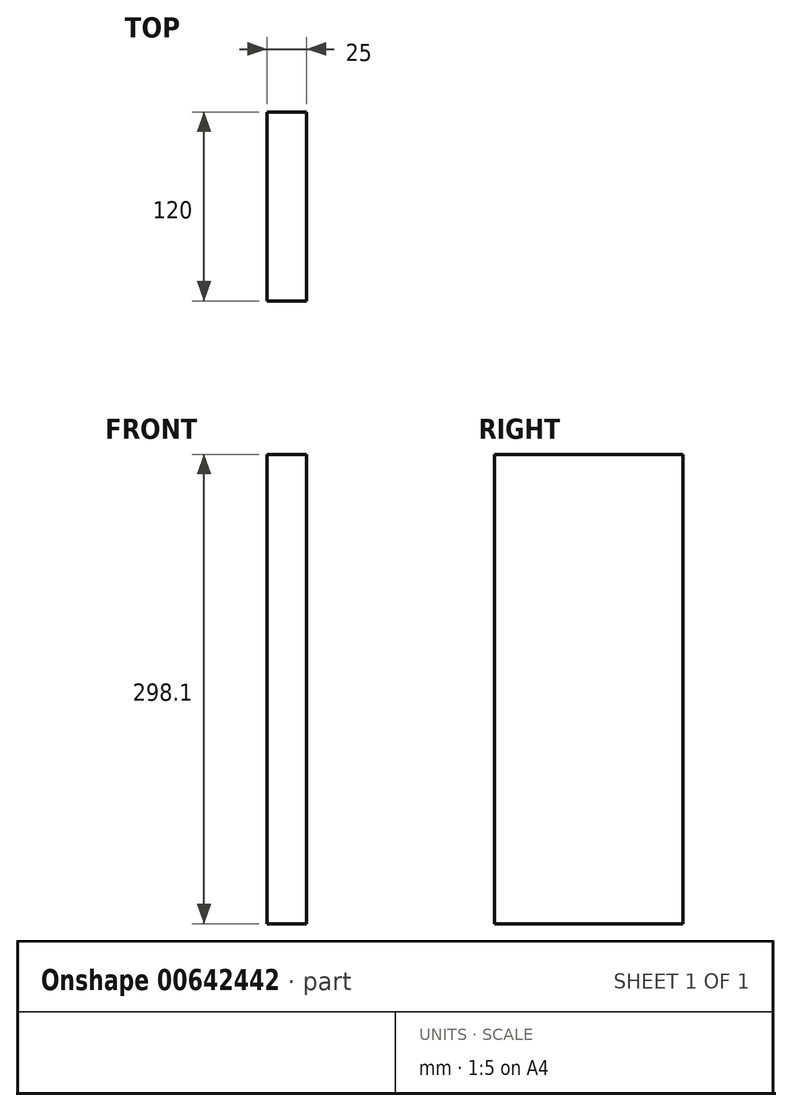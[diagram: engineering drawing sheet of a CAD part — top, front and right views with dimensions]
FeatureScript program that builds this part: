
annotation { "Feature Type Name" : "Feature", "Feature Type Description" : "" }
export const myFeature = defineFeature(function(context is Context, id is Id, definition is map)
    precondition{}
    {
        {
            var Q0;
            Q0=qCreatedBy(makeId("Right.planeOp"),FACE);
            var sketch = newSketch(context, id + "F0", { "sketchPlane" : qUnion([Q0])});
            skLineSegment(sketch, "E0.bottom", {"start": v(-60, 25) * mm, "end": v(60, 25) * mm});
            skLineSegment(sketch, "E0.top", {"start": v(-60, -25) * mm, "end": v(60, -25) * mm});
            skLineSegment(sketch, "E0.left", {"start": v(-60, 25) * mm, "end": v(-60, -25) * mm});
            skLineSegment(sketch, "E0.right", {"start": v(60, 25) * mm, "end": v(60, -25) * mm});
            skPoint(sketch, "E0.middle", {"position": v(0, 0) * mm});
            skSolve(sketch);
        }
        {
            var Q0;
            Q0=makeQuery(id+"F0.imprint","IMPRINT",FACE,{"disambiguationData":[TD([[makeQuery(id+"F0.imprint","IMPRINT",EDGE,{"derivedFrom":sQuery(id+"F0.wireOp",EDGE,"E0.bottom")}),-1.0]])]});
            extrude(context, id + "F1", {"entities" : qUnion([Q0]), "depth" : 25 * mm, "offsetDistance" : 25 * mm});
        }
        {
            var Q0;
            Q0=makeQuery(id+"F1.opExtrude","SWEPT_FACE",FACE,{"disambiguationData":[OSD([sQuery(id+"F0.wireOp",EDGE,"E0.bottom")])]});
            extrude(context, id + "F2", {"entities" : qUnion([Q0]), "operationType" : NewBodyOperationType.ADD, "depth" : 250 * mm, "offsetDistance" : 25 * mm});
        }
        {
            var Q0;
            Q0=makeQuery(id+"F1.opExtrude","SWEPT_FACE",FACE,{"disambiguationData":[OSD([sQuery(id+"F0.wireOp",EDGE,"E0.top")])]});
            extrude(context, id + "F3", {"entities" : qUnion([Q0]), "operationType" : NewBodyOperationType.REMOVE, "oppositeDirection" : true, "depth" : 1.9 * mm, "offsetDistance" : 25 * mm});
        }
    });
